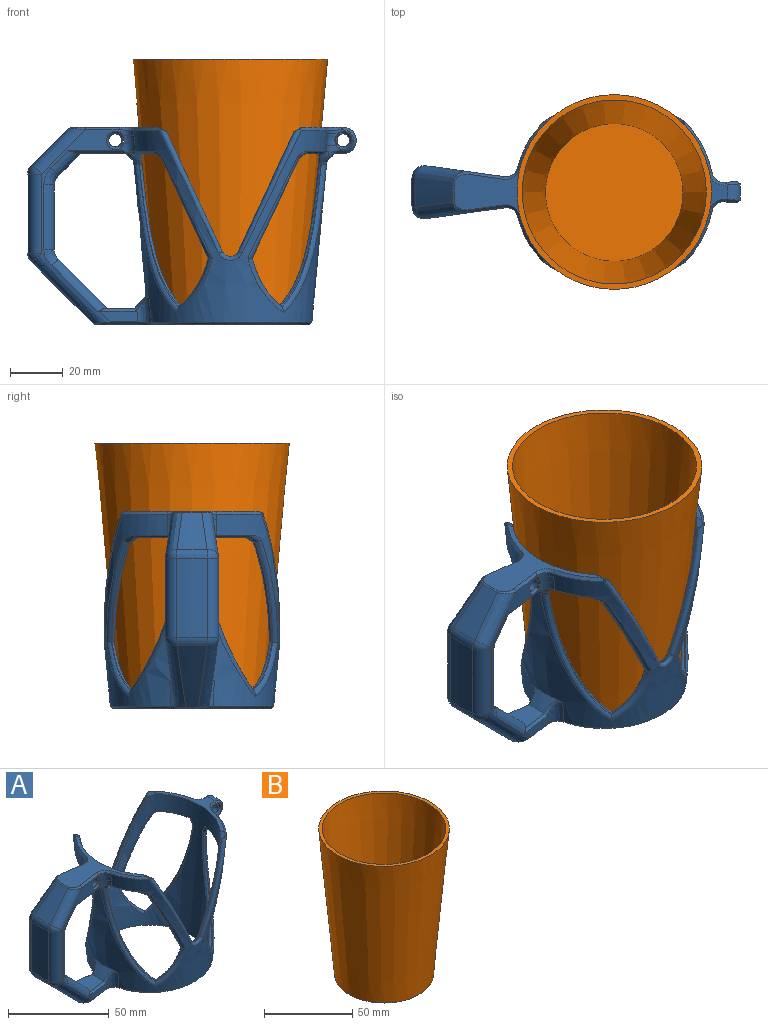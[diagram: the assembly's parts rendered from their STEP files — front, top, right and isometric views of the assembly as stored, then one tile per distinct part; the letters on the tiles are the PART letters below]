
ASSEMBLY  parts=2 mates=1
PART A: 228 faces, bbox 140.5x76.5x135.9 mm
  f0: bspline ~6.23x4.95mm, area 4.7mm2, adj f2,f50,f102,f172
  f1: bspline ~6.23x4.93mm, area 4.7mm2, adj f3,f49,f98,f174
  f2: plane 17.01x10.65mm, normal (0,0,-1), area 34.7mm2, adj f0,f16,f50,f51,f131,f172,f223,f227
  f3: plane 17.01x10.65mm, normal (0,0,-1), area 34.7mm2, adj f1,f16,f49,f56,f125,f174,f213,f217
  f4: plane 15.03x4.43mm, normal (0.14,-0.99,0), area 50.2mm2, adj f94,f105,f162,f200
  f5: plane 48.05x30.51mm, normal (0.14,0.99,0), area 144.5mm2, adj f74,f78,f79,f81,f87,f88,f92,f98
  f6: plane 20.01x15.28mm, normal (0,0,-1), area 202.8mm2, adj f32,f58,f78,f85,f130,f136,f170,f171
  f7: cone r=31mm half-angle=5.3deg, axis (0,0,1), area 5288.5mm2, adj f8,f57,f58,f61,f62,f63,f64,f65
  f8: cone r=31mm half-angle=5.3deg, axis (0,0,1), area 0.3mm2, adj f7,f57,f113
  f9: cylinder r=109.53mm len=54.38mm, axis (-1,0,0), area 16.6mm2, adj f41,f48,f109,f110,f218,f219
  f10: cylinder r=109.53mm len=54.38mm, axis (-1,0,0), area 16.7mm2, adj f40,f67,f118,f119,f211,f212
  f11: cylinder r=109.53mm len=54.38mm, axis (-1,0,0), area 16.6mm2, adj f42,f49,f127,f128,f213,f214
  f12: cylinder r=109.53mm len=54.38mm, axis (-1,0,0), area 16.6mm2, adj f39,f50,f133,f134,f223,f224
  f13: plane 12.88x12.32mm, normal (0,0,1), area 100.6mm2, adj f30,f89,f93,f106,f196,f197,f199,f200
  f14: plane 17x9.58mm, normal (0,0,-1), area 33.7mm2, adj f16,f52,f67,f116,f120,f176,f177,f208
  f15: plane 81.61x60.24mm, normal (0,0,-1), area 584.3mm2, adj f16,f162,f163,f164,f165,f166,f167,f168
  f16: cone r=28mm half-angle=5.3deg, axis (0,0,1), area 6303.9mm2, adj f2,f3,f14,f15,f17,f18,f27,f53
  f17: plane 50.37x33.86mm, normal (0,0,1), area 379.7mm2, adj f16,f54,f59,f138,f139,f140,f141,f142
  f18: plane 50.33x16.02mm, normal (0,0,1), area 140.6mm2, adj f16,f44,f53,f60,f151,f152,f153,f158
  f19: plane 45.37x21.15mm, normal (-0.91,0,0.42), area 23.6mm2, adj f20,f53,f63,f207
  f20: cylinder r=3.31mm len=6mm, axis (0,-1,0), area 4mm2, adj f19,f21,f62,f206
  f21: plane 45.37x21.15mm, normal (0.91,0,0.42), area 23.6mm2, adj f20,f54,f61,f205
  f22: plane 45.37x21.15mm, normal (0.91,0,0.42), area 23.6mm2, adj f23,f59,f66,f204
  f23: cylinder r=3.31mm len=6mm, axis (0,-1,0), area 4mm2, adj f22,f24,f65,f203
  f24: plane 45.37x21.15mm, normal (-0.91,0,0.42), area 23.6mm2, adj f23,f60,f64,f202
  f25: plane 38.09x17.8mm, normal (0.91,0,-0.42), area 22.9mm2, adj f40,f52,f116,f117,f118,f209
  f26: plane 38.09x17.8mm, normal (0.91,0,-0.42), area 22.9mm2, adj f41,f55,f107,f108,f109,f221
  f27: plane 17x9.58mm, normal (0,0,-1), area 33.7mm2, adj f16,f48,f55,f107,f112,f178,f179,f218
  f28: plane 38.09x17.8mm, normal (-0.91,0,-0.42), area 22.9mm2, adj f42,f56,f125,f126,f127,f216
  f29: plane 38.09x17.8mm, normal (-0.91,0,-0.42), area 22.9mm2, adj f39,f51,f131,f132,f133,f226
  f30: cone r=46.56mm half-angle=45deg, axis (0,0,1), area 184.8mm2, adj f13,f89,f93,f96
  f31: cylinder r=67.07mm len=24.68mm, axis (0,0,-1), area 249.6mm2, adj f86,f87,f95,f96
  f32: cone r=57.07mm half-angle=45deg, axis (0,0,-1), area 102.5mm2, adj f6,f78,f85,f86
  f33: cone r=61.21mm half-angle=45deg, axis (0,0,-1), area 189.3mm2, adj f74,f76,f77,f142
  f34: cylinder r=77.07mm len=30.14mm, axis (0,0,-1), area 353.5mm2, adj f76,f79,f83,f84
  f35: torus R=44mm, axis (0,0,-1), area 162.4mm2, adj f188,f189,f190,f191,f192,f193,f194,f195
  f36: cone r=77.07mm half-angle=45deg, axis (0,0,1), area 262.9mm2, adj f83,f88,f94,f165
  f37: plane 48.05x30.51mm, normal (0.14,-0.99,0), area 144.5mm2, adj f77,f84,f85,f91,f94,f95,f97,f102
  f38: plane 15.03x4.43mm, normal (0.14,0.99,0), area 50.1mm2, adj f88,f101,f169,f197
  f39: cylinder r=32.9mm len=18.34mm, axis (0,1,0), area 6mm2, adj f12,f29,f133,f224,f225,f226
  f40: cylinder r=32.9mm len=18.34mm, axis (0,1,0), area 6mm2, adj f10,f25,f118,f209,f210,f211
  f41: cylinder r=32.9mm len=18.34mm, axis (0,-1,0), area 6mm2, adj f9,f26,f109,f219,f220,f221
  f42: cylinder r=32.9mm len=18.34mm, axis (0,-1,0), area 6mm2, adj f11,f28,f127,f214,f215,f216
  f43: plane 5.55x3.32mm, normal (0,0,-1), area 16.4mm2, adj f44,f57,f111,f121,f148,f149,f155,f156
  f44: torus R=43mm, axis (0,0,-1), area 92.9mm2, adj f18,f43,f150,f157
  f45: torus R=43mm, axis (0,0,-1), area 89.1mm2, adj f180,f181,f182,f183,f184,f185,f186,f187
  f46: plane 8.02x5.46mm, normal (-0.09,1,0), area 7.1mm2, adj f68,f70,f156,f157,f158,f180
  f47: plane 8.02x5.46mm, normal (-0.09,-1,0), area 7.1mm2, adj f71,f73,f149,f150,f151,f185
  f48: plane 4.07x1.85mm, normal (0,0.91,-0.41), area 3mm2, adj f9,f27,f110,f112,f113,f115,f218
  f49: plane 5.14x3.72mm, normal (0,0.91,-0.41), area 5.3mm2, adj f1,f3,f11,f98,f128,f129,f130,f213
  f50: plane 5.14x3.72mm, normal (0,-0.91,-0.41), area 5.3mm2, adj f0,f2,f12,f102,f134,f135,f136,f223
  f51: plane 3.84x2.91mm, normal (-0.54,0,-0.84), area 2.5mm2, adj f2,f29,f131,f226,f227
  f52: plane 3.84x2.91mm, normal (0.54,0,-0.84), area 2.5mm2, adj f14,f25,f116,f208,f209
  f53: plane 5.04x3.21mm, normal (-0.54,0,0.84), area 9.5mm2, adj f16,f18,f19,f63,f153,f154,f207
  f54: plane 5.04x3.2mm, normal (0.54,0,0.84), area 9.5mm2, adj f16,f17,f21,f61,f137,f138,f205
  f55: plane 3.84x2.91mm, normal (0.54,0,-0.84), area 2.5mm2, adj f26,f27,f107,f221,f222
  f56: plane 3.84x2.91mm, normal (-0.54,0,-0.84), area 2.5mm2, adj f3,f28,f125,f216,f217
  f57: cone r=39.93mm half-angle=47.7deg, axis (0,0,1), area 26.3mm2, adj f7,f8,f43,f111,f113,f115,f121,f122
  f58: cone r=39.93mm half-angle=47.7deg, axis (0,0,1), area 34.2mm2, adj f6,f7,f129,f130,f135,f136
  f59: plane 5.04x3.21mm, normal (0.54,0,0.84), area 9.5mm2, adj f16,f17,f22,f66,f146,f147,f204
  f60: plane 5.04x3.2mm, normal (-0.54,0,0.84), area 9.5mm2, adj f16,f18,f24,f64,f160,f161,f202
  f61: bspline ~58.8x29mm, area 146.8mm2, adj f7,f21,f54,f62,f137
  f62: bspline ~9.62x4.15mm, area 20.8mm2, adj f7,f20,f61,f63
  f63: bspline ~58.8x29mm, area 146.8mm2, adj f7,f19,f53,f62,f154
  f64: bspline ~58.8x29mm, area 146.8mm2, adj f7,f24,f60,f65,f161
  f65: bspline ~9.62x4.15mm, area 20.8mm2, adj f7,f23,f64,f66
  f66: bspline ~58.8x29mm, area 146.8mm2, adj f7,f22,f59,f65,f147
  f67: plane 4.07x1.85mm, normal (0,-0.91,-0.41), area 3mm2, adj f10,f14,f119,f120,f122,f124,f212
  f68: bspline ~64.17x10.85mm, area 15.8mm2, adj f7,f46,f69,f111,f112,f155,f179,f182
  f69: bspline ~5.48x5.35mm, area 20.8mm2, adj f7,f68,f70,f183
  f70: bspline ~51.42x9.66mm, area 8.7mm2, adj f7,f46,f69,f159,f181
  f71: bspline ~64.17x10.85mm, area 15.8mm2, adj f7,f47,f72,f120,f121,f148,f177,f184
  f72: bspline ~5.48x5.35mm, area 20.7mm2, adj f7,f71,f73,f186
  f73: bspline ~51.42x9.66mm, area 8.7mm2, adj f7,f47,f72,f152,f187
  f74: bspline ~42.26x42.14mm, area 163.6mm2, adj f5,f33,f75,f143
  f75: sphere r=4.6mm, area 12.9mm2, adj f74,f76,f79
  f76: torus R=72.47mm, axis (0,0,1), area 42.1mm2, adj f33,f34,f75,f80
  f77: bspline ~44.52x44.42mm, area 163.6mm2, adj f33,f37,f80,f141
  f78: bspline ~43.84x43.29mm, area 74.7mm2, adj f5,f6,f32,f81,f173
  f79: cylinder r=4.6mm len=30.14mm, axis (0,0,-1), area 226.6mm2, adj f5,f34,f75,f82
  f80: sphere r=4.6mm, area 12.9mm2, adj f76,f77,f84
  f81: bspline ~8.84x6.62mm, area 34.6mm2, adj f5,f78,f86,f87
  f82: sphere r=4.6mm, area 12.9mm2, adj f79,f83,f88
  f83: torus R=72.47mm, axis (0,0,1), area 42.1mm2, adj f34,f36,f82,f90
  f84: cylinder r=4.6mm len=30.14mm, axis (0,0,-1), area 226.6mm2, adj f34,f37,f80,f90
  f85: bspline ~34.82x34.37mm, area 74.7mm2, adj f6,f32,f37,f91,f170
  f86: torus R=62.47mm, axis (0,0,-1), area 35.7mm2, adj f31,f32,f81,f91
  f87: cylinder r=4.6mm len=24.68mm, axis (0,0,-1), area 171.1mm2, adj f5,f31,f81,f92
  f88: bspline ~45.86x45.79mm, area 244mm2, adj f5,f36,f38,f82,f89,f92,f167,f198
  f89: bspline ~38.5x38mm, area 162.9mm2, adj f13,f30,f88,f92,f197,f198
  f90: sphere r=4.6mm, area 12.9mm2, adj f83,f84,f94
  f91: bspline ~9.25x6.15mm, area 34.6mm2, adj f37,f85,f86,f95
  f92: bspline ~9.25x6.15mm, area 33.2mm2, adj f5,f87,f88,f89,f96
  f93: bspline ~40.57x40.05mm, area 162.9mm2, adj f13,f30,f94,f97,f200,f201
  f94: bspline ~52.17x52.17mm, area 244mm2, adj f4,f36,f37,f90,f93,f97,f163,f201
  f95: cylinder r=4.6mm len=24.68mm, axis (0,0,-1), area 171.1mm2, adj f31,f37,f91,f97
  f96: torus R=62.47mm, axis (0,0,-1), area 35.7mm2, adj f30,f31,f92,f97
  f97: bspline ~8.84x6.62mm, area 33.2mm2, adj f37,f93,f94,f95,f96
  f98: bspline ~102.5x14.55mm, area 21.8mm2, adj f1,f5,f7,f49,f99,f130,f175,f189
  f99: bspline ~5.56x4.17mm, area 15.2mm2, adj f7,f98,f100,f191
  f100: bspline ~51.46x9.82mm, area 13.9mm2, adj f5,f7,f99,f145,f190
  f101: bspline ~51.39x9.8mm, area 51mm2, adj f7,f38,f168,f196
  f102: bspline ~102.5x14.55mm, area 21.8mm2, adj f0,f7,f37,f50,f103,f136,f171,f195
  f103: bspline ~5.56x4.17mm, area 15.2mm2, adj f7,f102,f104,f194
  f104: bspline ~51.46x9.82mm, area 13.9mm2, adj f7,f37,f103,f139,f192
  f105: bspline ~51.39x9.8mm, area 51mm2, adj f4,f7,f164,f199
  f106: cone r=32.02mm half-angle=42.3deg, axis (0,0,-1), area 73.8mm2, adj f7,f13,f196,f199
  f107: bspline ~9.84x9mm, area 10.3mm2, adj f7,f26,f27,f55,f108,f178
  f108: bspline ~46.89x23.16mm, area 94.4mm2, adj f7,f26,f107,f109
  f109: bspline ~23.74x15.96mm, area 65.5mm2, adj f7,f9,f26,f41,f108,f110
  f110: bspline ~60.55x23.06mm, area 163.7mm2, adj f7,f9,f48,f109,f113
  f111: bspline ~4.37x3.62mm, area 6.9mm2, adj f43,f57,f68,f114,f155
  f112: bspline ~3.92x2.25mm, area 3.4mm2, adj f27,f48,f68,f114,f179
  f113: bspline ~28.08x14.37mm, area 3.9mm2, adj f8,f48,f57,f110,f115
  f114: sphere r=2mm, area 1.5mm2, adj f111,f112,f115
  f115: bspline ~10.83x9.89mm, area 3.7mm2, adj f48,f57,f113,f114
  f116: bspline ~9.84x9mm, area 10.3mm2, adj f7,f14,f25,f52,f117,f176
  f117: bspline ~46.89x23.16mm, area 94.4mm2, adj f7,f25,f116,f118
  f118: bspline ~25.41x17.69mm, area 65.5mm2, adj f7,f10,f25,f40,f117,f119
  f119: bspline ~60.55x23.06mm, area 163.7mm2, adj f7,f10,f67,f118,f122
  f120: bspline ~3.92x2.25mm, area 3.4mm2, adj f14,f67,f71,f123,f177
  f121: bspline ~4.58x3.86mm, area 6.9mm2, adj f43,f57,f71,f123,f148
  f122: bspline ~28.08x14.37mm, area 3.9mm2, adj f7,f57,f67,f119,f124
  f123: sphere r=2mm, area 1.5mm2, adj f120,f121,f124
  f124: bspline ~10.83x9.89mm, area 3.7mm2, adj f57,f67,f122,f123
  f125: bspline ~9.84x9mm, area 10.3mm2, adj f3,f7,f28,f56,f126,f174
  f126: bspline ~46.89x23.16mm, area 94.4mm2, adj f7,f28,f125,f127
  f127: bspline ~25.41x17.69mm, area 65.5mm2, adj f7,f11,f28,f42,f126,f128
  f128: bspline ~60.55x23.06mm, area 163.7mm2, adj f7,f11,f49,f127,f129
  f129: bspline ~28.08x14.37mm, area 3.9mm2, adj f7,f49,f58,f128,f130
  f130: bspline ~10.95x10.02mm, area 12.1mm2, adj f6,f49,f58,f98,f129,f175
  f131: bspline ~9.84x9mm, area 10.3mm2, adj f2,f7,f29,f51,f132,f172
  f132: bspline ~46.89x23.16mm, area 94.4mm2, adj f7,f29,f131,f133
  f133: bspline ~23.74x15.96mm, area 65.5mm2, adj f7,f12,f29,f39,f132,f134
  f134: bspline ~60.55x23.06mm, area 163.7mm2, adj f7,f12,f50,f133,f135
  f135: bspline ~28.08x14.37mm, area 3.9mm2, adj f7,f50,f58,f134,f136
  f136: bspline ~14.04x12.93mm, area 12.2mm2, adj f6,f50,f58,f102,f135,f171
  f137: bspline ~1.2x1.17mm, area 0.5mm2, adj f54,f61,f138
  f138: cone r=36.9mm half-angle=42.3deg, axis (0,0,-1), area 28.9mm2, adj f7,f17,f54,f137,f139
  f139: bspline ~6.23x4.61mm, area 10.9mm2, adj f17,f104,f138,f140
  f140: plane 13.25x2.83mm, normal (0.1,-0.7,0.71), area 18.7mm2, adj f17,f37,f139,f141
  f141: bspline ~6.42x4.14mm, area 8.1mm2, adj f17,f77,f140,f142
  f142: cone r=61.5mm half-angle=67.5deg, axis (0,0,-1), area 5.7mm2, adj f17,f33,f141,f143
  f143: bspline ~6.42x4.14mm, area 8.1mm2, adj f17,f74,f142,f144
  f144: plane 13.25x2.83mm, normal (0.1,0.7,0.71), area 18.7mm2, adj f5,f17,f143,f145
  f145: bspline ~6.23x4.61mm, area 10.9mm2, adj f17,f100,f144,f146
  f146: cone r=36.9mm half-angle=42.3deg, axis (0,0,-1), area 28.9mm2, adj f7,f17,f59,f145,f147
  f147: bspline ~1.14x0.94mm, area 0.5mm2, adj f59,f66,f146
  f148: bspline ~4.02x2.12mm, area 3mm2, adj f43,f71,f121,f149
  f149: plane 1.54x1.12mm, normal (-0.06,-0.7,-0.71), area 2.1mm2, adj f43,f47,f148,f150
  f150: bspline ~10.01x5.07mm, area 20.1mm2, adj f44,f47,f149,f151
  f151: plane 1.06x1mm, normal (-0.06,-0.7,0.71), area 1mm2, adj f18,f47,f150,f152
  f152: bspline ~6.01x4.81mm, area 10.9mm2, adj f18,f73,f151,f153
  f153: cone r=36.9mm half-angle=42.3deg, axis (0,0,-1), area 31.8mm2, adj f7,f18,f53,f152,f154
  f154: bspline ~1.14x0.94mm, area 0.5mm2, adj f53,f63,f153
  f155: bspline ~4.02x2.12mm, area 3mm2, adj f43,f68,f111,f156
  f156: plane 1.54x1.12mm, normal (-0.06,0.7,-0.71), area 2.1mm2, adj f43,f46,f155,f157
  f157: bspline ~10.01x5.07mm, area 20.1mm2, adj f44,f46,f156,f158
  f158: plane 1.06x1mm, normal (-0.06,0.7,0.71), area 1mm2, adj f18,f46,f157,f159
  f159: bspline ~6.01x4.81mm, area 10.9mm2, adj f18,f70,f158,f160
  f160: cone r=36.9mm half-angle=42.3deg, axis (0,0,-1), area 31.8mm2, adj f7,f18,f60,f159,f161
  f161: bspline ~1.13x0.93mm, area 0.5mm2, adj f60,f64,f160
  f162: plane 10.76x2.48mm, normal (0.1,-0.7,-0.71), area 15.2mm2, adj f4,f15,f163,f164
  f163: bspline ~6.42x4.18mm, area 8.1mm2, adj f15,f94,f162,f165
  f164: bspline ~6.2x4.51mm, area 10.1mm2, adj f15,f105,f162,f166
  f165: cone r=51.46mm half-angle=67.5deg, axis (0,0,1), area 3.6mm2, adj f15,f36,f163,f167
  f166: cone r=31.08mm half-angle=47.7deg, axis (0,0,1), area 236.7mm2, adj f7,f15,f164,f168
  f167: bspline ~6.42x4.18mm, area 8.1mm2, adj f15,f88,f165,f169
  f168: bspline ~6.2x4.51mm, area 10.1mm2, adj f15,f101,f166,f169
  f169: plane 10.76x2.48mm, normal (0.1,0.7,-0.71), area 15.2mm2, adj f15,f38,f167,f168
  f170: plane 21.41x4.64mm, normal (0.1,-0.7,-0.71), area 26.3mm2, adj f6,f37,f85,f171
  f171: bspline ~1.63x1.05mm, area 1.5mm2, adj f6,f102,f136,f170
  f172: cone r=36.16mm half-angle=47.7deg, axis (0,0,1), area 19.5mm2, adj f0,f2,f7,f131
  f173: plane 21.41x4.63mm, normal (0.1,0.7,-0.71), area 26.3mm2, adj f5,f6,f78,f175
  f174: cone r=36.16mm half-angle=47.7deg, axis (0,0,1), area 19.5mm2, adj f1,f3,f7,f125
  f175: bspline ~5.05x2.54mm, area 1.6mm2, adj f6,f98,f130,f173
  f176: cone r=36.16mm half-angle=47.7deg, axis (0,0,1), area 22.1mm2, adj f7,f14,f116,f177
  f177: bspline ~2.77x2.02mm, area 2.1mm2, adj f14,f71,f120,f176
  f178: cone r=36.16mm half-angle=47.7deg, axis (0,0,1), area 22.1mm2, adj f7,f27,f107,f179
  f179: bspline ~2.35x1.75mm, area 2mm2, adj f27,f68,f112,f178
  f180: bspline ~7.32x4.91mm, area 15.9mm2, adj f45,f46,f181,f182
  f181: bspline ~1.72x1.64mm, area 2.1mm2, adj f45,f70,f180,f183
  f182: bspline ~1.79x1.7mm, area 2.1mm2, adj f45,f68,f180,f183
  f183: bspline ~4.48x1.4mm, area 4.4mm2, adj f45,f69,f181,f182
  f184: bspline ~1.79x1.7mm, area 2.1mm2, adj f45,f71,f185,f186
  f185: bspline ~7.32x4.91mm, area 15.9mm2, adj f45,f47,f184,f187
  f186: bspline ~4.48x1.4mm, area 4.4mm2, adj f45,f72,f184,f187
  f187: bspline ~1.72x1.64mm, area 2.1mm2, adj f45,f73,f185,f186
  f188: bspline ~7.06x5.82mm, area 18.7mm2, adj f5,f35,f189,f190
  f189: bspline ~1.85x1.6mm, area 2.1mm2, adj f35,f98,f188,f191
  f190: bspline ~1.81x1.72mm, area 2mm2, adj f35,f100,f188,f191
  f191: bspline ~2.73x1.29mm, area 2.9mm2, adj f35,f99,f189,f190
  f192: bspline ~1.81x1.72mm, area 2mm2, adj f35,f104,f193,f194
  f193: bspline ~7.07x5.82mm, area 18.7mm2, adj f35,f37,f192,f195
  f194: bspline ~2.73x1.29mm, area 2.9mm2, adj f35,f103,f192,f195
  f195: bspline ~1.85x1.6mm, area 2mm2, adj f35,f102,f193,f194
  f196: bspline ~6.32x6.02mm, area 9.1mm2, adj f7,f13,f101,f106,f197
  f197: plane 14.26x3.16mm, normal (0.1,0.7,0.71), area 18.7mm2, adj f13,f38,f89,f196,f198
  f198: bspline ~2.11x1.25mm, area 0.1mm2, adj f88,f89,f197
  f199: bspline ~6.32x6.02mm, area 9.1mm2, adj f7,f13,f105,f106,f200
  f200: plane 14.26x3.15mm, normal (0.1,-0.7,0.71), area 18.7mm2, adj f4,f13,f93,f199,f201
  f201: bspline ~2.11x1.25mm, area 0.1mm2, adj f93,f94,f200
  f202: bspline ~46.35x21.66mm, area 57.1mm2, adj f16,f24,f60,f203
  f203: bspline ~7.97x3.58mm, area 12mm2, adj f16,f23,f202,f204
  f204: bspline ~46.35x21.66mm, area 57.1mm2, adj f16,f22,f59,f203
  f205: bspline ~46.35x21.66mm, area 57.1mm2, adj f16,f21,f54,f206
  f206: bspline ~7.97x3.58mm, area 12mm2, adj f16,f20,f205,f207
  f207: bspline ~46.35x21.66mm, area 57.1mm2, adj f16,f19,f53,f206
  f208: bspline ~4.49x4.27mm, area 8.6mm2, adj f14,f16,f52,f209
  f209: bspline ~52.72x25.41mm, area 88.2mm2, adj f16,f25,f40,f52,f208,f210
  f210: bspline ~24.4x15.09mm, area 43.2mm2, adj f16,f40,f209,f211
  f211: bspline ~59.31x21.11mm, area 112.5mm2, adj f10,f16,f40,f210,f212
  f212: bspline ~4.81x2.95mm, area 7.4mm2, adj f10,f14,f16,f67,f211
  f213: bspline ~4.81x2.95mm, area 7.4mm2, adj f3,f11,f16,f49,f214
  f214: bspline ~57.8x21.33mm, area 112.5mm2, adj f11,f16,f42,f213,f215
  f215: bspline ~24.4x15.09mm, area 43.2mm2, adj f16,f42,f214,f216
  f216: bspline ~52.72x25.41mm, area 88.2mm2, adj f16,f28,f42,f56,f215,f217
  f217: bspline ~4.49x4.27mm, area 8.6mm2, adj f3,f16,f56,f216
  f218: bspline ~4.81x2.95mm, area 7.4mm2, adj f9,f16,f27,f48,f219
  f219: bspline ~59.31x21.11mm, area 112.5mm2, adj f9,f16,f41,f218,f220
  f220: bspline ~24.4x14.62mm, area 43.2mm2, adj f16,f41,f219,f221
  f221: bspline ~52.72x25.41mm, area 88.2mm2, adj f16,f26,f41,f55,f220,f222
  f222: bspline ~4.49x4.27mm, area 8.6mm2, adj f16,f27,f55,f221
  f223: bspline ~4.81x2.95mm, area 7.4mm2, adj f2,f12,f16,f50,f224
  f224: bspline ~57.8x21.33mm, area 112.5mm2, adj f12,f16,f39,f223,f225
  f225: bspline ~24.4x14.62mm, area 43.2mm2, adj f16,f39,f224,f226
  f226: bspline ~52.72x25.41mm, area 88.2mm2, adj f16,f29,f39,f51,f225,f227
  f227: bspline ~4.49x4.27mm, area 8.6mm2, adj f2,f16,f51,f226
PART B: 5 faces, bbox 74x74x101 mm
  f0: plane 56x56mm, normal (0,0,-1), area 2463mm2, adj f2
  f1: plane 74x74mm, normal (0,0,1), area 454.1mm2, adj f2,f4
  f2: cone r=28mm half-angle=5.1deg, axis (0,0,1), area 20706.3mm2, adj f0,f1
  f3: plane 52.34x52.34mm, normal (0,0,1), area 2151.6mm2, adj f4
  f4: cone r=26.01mm half-angle=5.1deg, axis (0,0,1), area 19098mm2, adj f1,f3
PLACE A t=(-18.29,10.8,-117.69)mm fixed
PLACE B t=(-18.29,10.8,-117.79)mm
MATE slider B.f2 <-> A.f16  axis (0,0,1) through (-18.29,10.8,-16.79)mm
